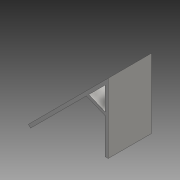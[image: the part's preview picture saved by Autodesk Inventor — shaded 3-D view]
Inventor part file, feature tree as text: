
AUTODESK INVENTOR PART (.ipt)
format: ipt  version: 2016 (Build 200138000, 138)  size: 100,864 bytes
history: native  units: mm
features: extrude x3, sketch x3, projected_geometry x2
ambient origin geometry x8: Origin, YZ Plane, XZ Plane, XY Plane, X Axis, Y Axis, Z Axis, Center Point
bodies: 实体1 (feature_tree)
feature tree (8):
  extrude  "拉伸1"  Depth=3.0mm
  extrude  "拉伸2"  Depth=3.0mm
  extrude  "拉伸3"  Depth=42.0mm TaperAngle=0.0deg
  sketch  "草图1"  dims[d2=45.0deg d3=60.0mm d4=3.0mm]
  sketch  "草图2"  dims[d5=67.5deg d6=3.0mm]
  projected_geometry  "投影回路1"
  sketch  "草图3"  dims[d7=42.0mm d8=0.0mm d9=42.0mm d10=0.0mm d11=30.0mm d12=21.0mm d13=21.0mm d14=42.0mm d15=0.0mm]
  projected_geometry  "投影回路2"
